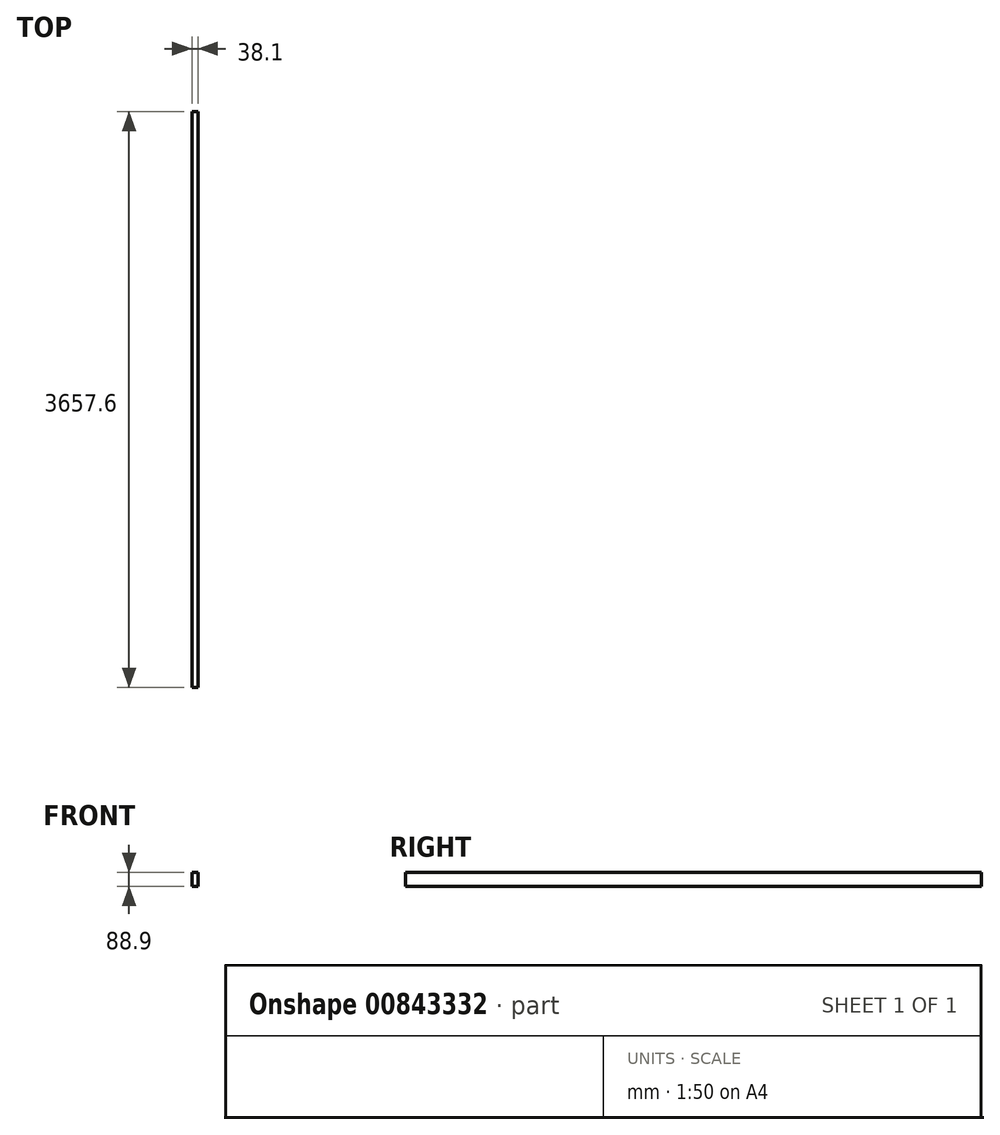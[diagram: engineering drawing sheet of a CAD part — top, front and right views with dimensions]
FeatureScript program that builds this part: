
annotation { "Feature Type Name" : "Feature", "Feature Type Description" : "" }
export const myFeature = defineFeature(function(context is Context, id is Id, definition is map)
    precondition{}
    {
        {
            var Q0;
            Q0=qCreatedBy(makeId("Front.planeOp"),FACE);
            var sketch = newSketch(context, id + "F0", { "sketchPlane" : qUnion([Q0])});
            skLineSegment(sketch, "E0.bottom", {"start": v(19.05, -44.45) * mm, "end": v(-19.05, -44.45) * mm});
            skLineSegment(sketch, "E0.top", {"start": v(19.05, 44.45) * mm, "end": v(-19.05, 44.45) * mm});
            skLineSegment(sketch, "E0.left", {"start": v(19.05, -44.45) * mm, "end": v(19.05, 44.45) * mm});
            skLineSegment(sketch, "E0.right", {"start": v(-19.05, -44.45) * mm, "end": v(-19.05, 44.45) * mm});
            skPoint(sketch, "E0.middle", {"position": v(0, 0) * mm});
            skSolve(sketch);
        }
        {
            var Q0;
            Q0=qSketchRegion(id+"F0",true);
            extrude(context, id + "F1", {"entities" : qUnion([Q0]), "depth" : 3657.6 * mm, "offsetDistance" : 25.4 * mm});
        }
    });
